# Revit family: Pnl_Furniture-Labgrade-ABET-16mm-3660x1610-M3_000000
name_source: partatom
category: Arredi
revit_build: Autodesk Revit 2016 (Build: 20150220_1215(x64)
units: mm (PartAtom-declared; Revit-internal decimal feet)

## family parameters
Basato su piano di lavoro = Sì
Condiviso = Sì
Numero OmniClass = 23.40.70.11.11
Punto di calcolo locali = No
Sempre verticale = No
Taglio con vuoti quando caricato = Sì
Titolo OmniClass = Laboratory Equipment and Furnishings

## types (1)
- 3660x1610mm
    ABET-Coeff_linear_thermal_expansion-L-ASTM_D_696 = 1,6 x 10^-5 ca °C-1
    ABET-Coeff_linear_thermal_expansion-T-ASTM_D_696 = 3,5 x  10^-5 ca  °C-1
    ABET-Density-ISO_1183 = ≥1,35 gr/cm3
    ABET-Electrical_R-EN_61340-4-1 = 1x10^9 - 1x10^11 Ohm
    ABET-Flatness-EN_438-2.9 = ≤3,0 mm/m
    ABET-Flexural_modulus-EN_ISO_178 = ≥9.000  Mpa
    ABET-Flexural_strength-EN_ISO_178 = ≥80  Mpa
    ABET-Length_Width-EN_438-2.6 = +10/0 mm
    ABET-Lightfastness-EN_438-2.27 = 4 scala grigi (min)
    ABET-R_cigarette_burns-EN_438-2.30 = 3 (min)
    ABET-R_dry_heat_180dC-EN_438-2.16 = 4 (min)
    ABET-R_imm_boiling_water-EN_438-2.12 = 4 (min)
    ABET-R_imm_boiling_water-M_incr-EN_438-2.12 = 2% (max)
    ABET-R_imm_boiling_water-Thickness_incr-EN_438-2.12 = 2% (max)
    ABET-R_impacy_La_D_ball-Drop_H-EN_438-2.21 = 1800 mm(min)
    ABET-R_impacy_La_D_ball-Indentation_D-EN_438-2.21 = 10 mm(max)
    ABET-R_scratching-EN_438-2.25 = 3 (min)
    ABET-R_surface_wear-Inial_point-EN_438-2.10 = ≥150 giri
    ABET-R_surface_wear-Wear_value-EN_438-2.10 = ≥350 giri
    ABET-R_water_vapour-EN_438-2.14 = 4 (min)
    ABET-R_wet_heat_100dC-EN_12721 = 4 (min)
    ABET-Squareness-EN_438-2.8 = 1,5 mm/m
    ABET-Stability_elevated_Temp-L-EN_438-2.17 = 0,3%
    ABET-Stability_elevated_Temp-T-EN_438-2.17 = 0,6%
    ABET-Straightness_edges-EN_438-2.7 = 1,5 mm/m
    ABET-Tensile_strength-EN_ISO_527-2 = ≥60 Mpa
    ABET-Thermal_Conductivity-DIN_52 612 = 0,25 W/m°K
    ABET-Thickness-EN_438-2.5 = ±0,7 mm
    ABET_Length = 3660 mm  [stored 12.0079 ft]
    ABET_Length_max = 3660 mm  [stored 12.0079 ft]
    ABET_Length_value = 3660 mm  [stored 12.0079 ft]
    ABET_Offset = 0 mm  [stored 0 ft]
    ABET_Thickness = 16 mm  [stored 0.0524934 ft]
    ABET_Width = 1610 mm  [stored 5.28215 ft]
    ABET_Width_max = 1610 mm  [stored 5.28215 ft]
    ABET_Width_value = 1610 mm  [stored 5.28215 ft]
    COBie_Cost = 0
    COBie_ExpectedLife = 0
    COBie_ReplacementCost = 0
    COBie_WarrantyDurationLabour = 0
    COBie_WarrantyDurationParts = 0
    Commenti sul tipo = 3660x1610mm
    Descrizione = Self-supporting material consisting of layers of kraft paper impregnated with thermosetting resins and layers of decorative paper impregnated with aminoplastic resins; all bonded together by means of high pressure (9 MPa) and heat (150 °C). The surface is nontoxic, chemically inert and physiologically safe. It is approved for use in contact with foodstuffs. For its outstanding resistance to chemicals, it is particularly suitable for applications in chemistry, physics, photographics, cosmetics, electronics and nuclear laboratories, for schools and industrial kitchens.
    IfcExportAs = IfcFurniture
    IfcExportType = NOTDEFINED
    Modello = Labgrade
    Produttore = Abet Laminati S.P.A.
    Prospetto di default = 0 mm  [stored 0 ft]
    Sys_URL(ManufacturerWebsite) = http://abetlaminati.com
    Sys_URL(TechnicalProductDataSheet) = http://abetlaminati.com
    Sys_URL(Use-and-MaintenanceManual) = http://abetlaminati.com
    URL = http://abetlaminati.com
    Uniclass2015_Code = Pr_25_71_63_15
    Uniclass_2015_Description = Compact or solid grade high-pressure laminate (HPL) boards

note: [stored X ft] marks values corroborated as IEEE doubles in the binary element streams (Revit-internal decimal feet)

## geometry (parser evidence)
native form markers: Sweep x3
no freeform markers — native parametric forms only
